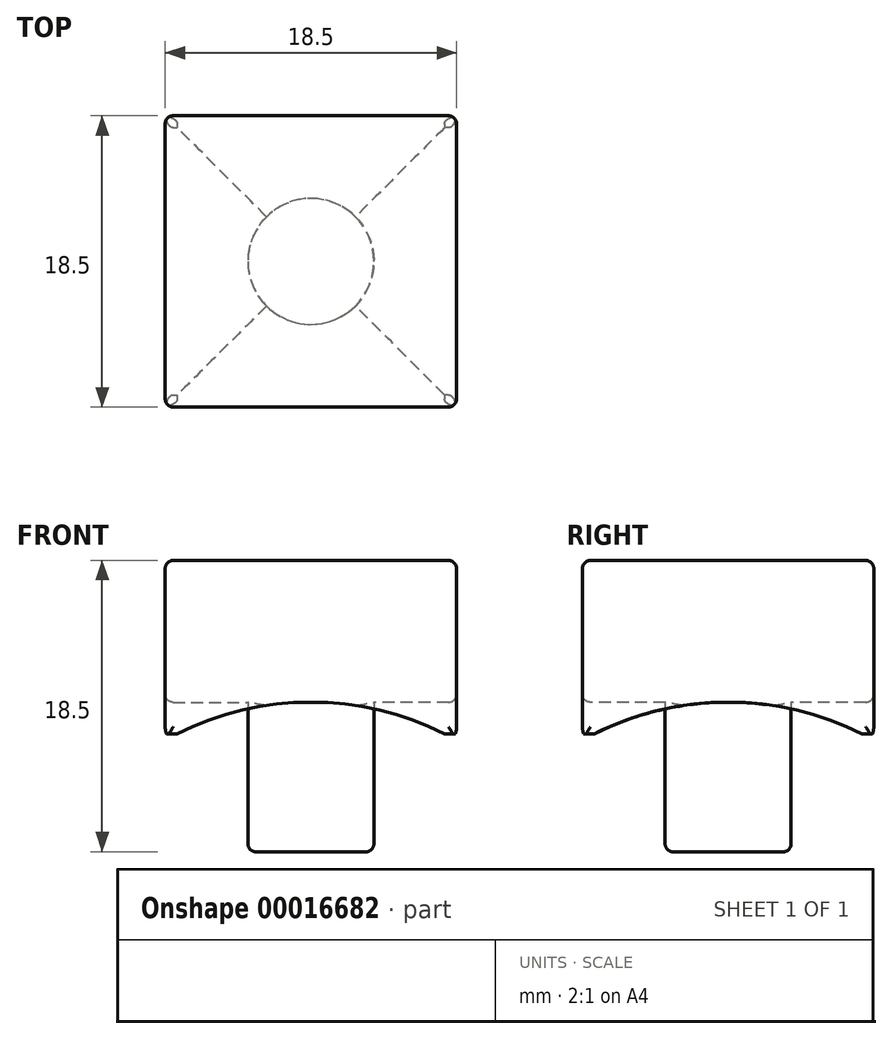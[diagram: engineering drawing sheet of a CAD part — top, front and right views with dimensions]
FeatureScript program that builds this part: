
annotation { "Feature Type Name" : "Feature", "Feature Type Description" : "" }
export const myFeature = defineFeature(function(context is Context, id is Id, definition is map)
    precondition{}
    {
        {
            var Q0;
            Q0=qCreatedBy(makeId("Front.planeOp"),FACE);
            var sketch = newSketch(context, id + "F0", { "sketchPlane" : qUnion([Q0])});
            skLineSegment(sketch, "E0.rect.bottom", {"start": v(9.25, 5.5) * mm, "end": v(-9.25, 5.5) * mm});
            skLineSegment(sketch, "E0.rect.top", {"start": v(9.25, -5.5) * mm, "end": v(-9.25, -5.5) * mm});
            skLineSegment(sketch, "E0.rect.left", {"start": v(9.25, 5.5) * mm, "end": v(9.25, -5.5) * mm});
            skLineSegment(sketch, "E0.rect.right", {"start": v(-9.25, 5.5) * mm, "end": v(-9.25, -5.5) * mm});
            skPoint(sketch, "E0.rect.middle", {"position": v(0, 0) * mm});
            skSolve(sketch);
        }
        {
            var Q0;
            Q0=makeQuery(id+"F0.imprint","IMPRINT",FACE,{"disambiguationData":[TD([[makeQuery(id+"F0.imprint","IMPRINT",EDGE,{"derivedFrom":sQuery(id+"F0.wireOp",EDGE,"E0.rect.bottom")}),1.0]])]});
            extrude(context, id + "F1", {"entities" : qUnion([Q0]), "oppositeDirection" : true, "depth" : 9.25 * mm});
        }
        {
            var Q0;
            Q0 = qSketchRegion(id + "F0", true);
            extrude(context, id + "F2", {"entities" : qUnion([Q0]), "operationType" : NewBodyOperationType.ADD, "depth" : 9.25 * mm});
        }
        {
            var Q0;
            Q0=qCreatedBy(makeId("Front.planeOp"),FACE);
            var sketch = newSketch(context, id + "F3", { "sketchPlane" : qUnion([Q0])});
            skPoint(sketch, "E1", {"position": v(0, -3.5) * mm});
            skCircle(sketch, "E2", {"center": v(0, -22.5) * mm, "radius": 19 * mm});
            skSolve(sketch);
        }
        {
            var Q0;
            Q0=qCreatedBy(makeId("Right.planeOp"),FACE);
            var sketch = newSketch(context, id + "F4", { "sketchPlane" : qUnion([Q0])});
            skPoint(sketch, "E3", {"position": v(0, -3.5) * mm});
            skCircle(sketch, "E4", {"center": v(0, -22.5) * mm, "radius": 19 * mm});
            skSolve(sketch);
        }
        {
            var Q0;
            Q0 = qSketchRegion(id + "F9", true);
            var Q1;
            Q1 = qSketchRegion(id + "F3", true);
            extrude(context, id + "F5", {"entities" : qUnion([Q0, Q1]), "operationType" : NewBodyOperationType.REMOVE, "oppositeDirection" : true, "depth" : 25.4 * mm});
        }
        {
            var Q0;
            Q0 = qSketchRegion(id + "F3", true);
            extrude(context, id + "F6", {"entities" : qUnion([Q0]), "operationType" : NewBodyOperationType.REMOVE, "depth" : 25.4 * mm});
        }
        {
            var Q0;
            Q0 = qSketchRegion(id + "F4", true);
            extrude(context, id + "F7", {"entities" : qUnion([Q0]), "operationType" : NewBodyOperationType.REMOVE, "oppositeDirection" : true, "depth" : 25.4 * mm});
        }
        {
            var Q0;
            Q0 = qSketchRegion(id + "F4", true);
            extrude(context, id + "F8", {"entities" : qUnion([Q0]), "operationType" : NewBodyOperationType.REMOVE, "depth" : 25.4 * mm});
        }
        {
            var Q0;
            {var subQ0=sQuery(id+"F0.wireOp",EDGE,"E0.rect.top");Q0=makeQuery(id+"F2.boolean.opBoolean","MERGE",FACE,{"derivedFrom":[makeQuery(id+"F1.opExtrude","SWEPT_FACE",FACE,{"disambiguationData":[OSD([subQ0])]}),makeQuery(id+"F2.opExtrude","SWEPT_FACE",FACE,{"disambiguationData":[OSD([subQ0])]})]});}
            var sketch = newSketch(context, id + "F9", { "sketchPlane" : qUnion([Q0])});
            skCircle(sketch, "E5", {"center": v(0, 0) * mm, "radius": 4 * mm});
            skSolve(sketch);
        }
        {
            var Q0;
            Q0 = qSketchRegion(id + "F9", true);
            extrude(context, id + "F10", {"entities" : qUnion([Q0]), "operationType" : NewBodyOperationType.ADD, "oppositeDirection" : true, "depth" : 3.46 * mm});
        }
        {
            var Q0;
            Q0=makeQuery(id+"F10.opExtrude","CAP_FACE",FACE,{"disambiguationData":[OSD([sQuery(id+"F9.wireOp",EDGE,"E5")])],"isStart":true});
            extrude(context, id + "F11", {"entities" : qUnion([Q0]), "operationType" : NewBodyOperationType.ADD, "depth" : 7.5 * mm});
        }
        {
            var Q0;
            Q0=makeQuery(id+"F2.opExtrude","CAP_EDGE",EDGE,{"disambiguationData":[OSD([sQuery(id+"F0.wireOp",EDGE,"E0.rect.left")])],"isStart":false});
            var Q1;
            Q1=makeQuery(id+"F2.opExtrude","CAP_EDGE",EDGE,{"disambiguationData":[OSD([sQuery(id+"F0.wireOp",EDGE,"E0.rect.bottom")])],"isStart":false});
            var Q2;
            {var subQ0=sQuery(id+"F0.wireOp",EDGE,"E0.rect.bottom");var subQ1=sQuery(id+"F0.wireOp",EDGE,"E0.rect.left");Q2=makeQuery(id+"F2.boolean.opBoolean","MERGE",EDGE,{"derivedFrom":[makeQuery(id+"F1.opExtrude","SWEPT_EDGE",EDGE,{"disambiguationData":[OSD([subQ0,subQ1])]}),makeQuery(id+"F2.opExtrude","SWEPT_EDGE",EDGE,{"disambiguationData":[OSD([subQ0,subQ1])]})]});}
            var Q3;
            Q3=makeQuery(id+"F1.opExtrude","CAP_EDGE",EDGE,{"disambiguationData":[OSD([sQuery(id+"F0.wireOp",EDGE,"E0.rect.bottom")])],"isStart":false});
            var Q4;
            {var subQ0=sQuery(id+"F0.wireOp",EDGE,"E0.rect.bottom");var subQ1=sQuery(id+"F0.wireOp",EDGE,"E0.rect.right");Q4=makeQuery(id+"F2.boolean.opBoolean","MERGE",EDGE,{"derivedFrom":[makeQuery(id+"F1.opExtrude","SWEPT_EDGE",EDGE,{"disambiguationData":[OSD([subQ0,subQ1])]}),makeQuery(id+"F2.opExtrude","SWEPT_EDGE",EDGE,{"disambiguationData":[OSD([subQ0,subQ1])]})]});}
            var Q5;
            Q5=makeQuery(id+"F2.opExtrude","CAP_EDGE",EDGE,{"disambiguationData":[OSD([sQuery(id+"F0.wireOp",EDGE,"E0.rect.right")])],"isStart":false});
            var Q6;
            Q6=makeQuery(id+"F1.opExtrude","CAP_EDGE",EDGE,{"disambiguationData":[OSD([sQuery(id+"F0.wireOp",EDGE,"E0.rect.left")])],"isStart":false});
            var Q7;
            Q7=makeQuery(id+"F1.opExtrude","CAP_EDGE",EDGE,{"disambiguationData":[OSD([sQuery(id+"F0.wireOp",EDGE,"E0.rect.right")])],"isStart":false});
            var Q8;
            Q8=makeQuery(id+"F11.opExtrude","CAP_EDGE",EDGE,{"disambiguationData":[OSD([sQuery(id+"F9.wireOp",EDGE,"E5")])],"isStart":false});
            var Q9;
            Q9=makeQuery(id+"F6.boolean.opBoolean","INTERSECT",EDGE,{"derivedFrom":[makeQuery(id+"F2.opExtrude","CAP_FACE",FACE,{"disambiguationData":[OSD([sQuery(id+"F0.wireOp",EDGE,"E0.rect.bottom"),sQuery(id+"F0.wireOp",EDGE,"E0.rect.top"),sQuery(id+"F0.wireOp",EDGE,"E0.rect.left"),sQuery(id+"F0.wireOp",EDGE,"E0.rect.right")])],"isStart":false}),makeQuery(id+"F6.opExtrude","SWEPT_FACE",FACE,{"disambiguationData":[OSD([sQuery(id+"F3.wireOp",EDGE,"E2")])]})]});
            var Q10;
            {var subQ0=sQuery(id+"F0.wireOp",EDGE,"E0.rect.right");Q10=makeQuery(id+"F7.boolean.opBoolean","INTERSECT",EDGE,{"derivedFrom":[makeQuery(id+"F2.boolean.opBoolean","MERGE",FACE,{"derivedFrom":[makeQuery(id+"F1.opExtrude","SWEPT_FACE",FACE,{"disambiguationData":[OSD([subQ0])]}),makeQuery(id+"F2.opExtrude","SWEPT_FACE",FACE,{"disambiguationData":[OSD([subQ0])]})]}),makeQuery(id+"F7.opExtrude","SWEPT_FACE",FACE,{"disambiguationData":[OSD([sQuery(id+"F4.wireOp",EDGE,"E4")])]})]});}
            var Q11;
            {var subQ0=sQuery(id+"F0.wireOp",EDGE,"E0.rect.left");Q11=makeQuery(id+"F8.boolean.opBoolean","INTERSECT",EDGE,{"derivedFrom":[makeQuery(id+"F2.boolean.opBoolean","MERGE",FACE,{"derivedFrom":[makeQuery(id+"F1.opExtrude","SWEPT_FACE",FACE,{"disambiguationData":[OSD([subQ0])]}),makeQuery(id+"F2.opExtrude","SWEPT_FACE",FACE,{"disambiguationData":[OSD([subQ0])]})]}),makeQuery(id+"F8.opExtrude","SWEPT_FACE",FACE,{"disambiguationData":[OSD([sQuery(id+"F4.wireOp",EDGE,"E4")])]})]});}
            var Q12;
            Q12=makeQuery(id+"F5.boolean.opBoolean","INTERSECT",EDGE,{"derivedFrom":[makeQuery(id+"F1.opExtrude","CAP_FACE",FACE,{"disambiguationData":[OSD([sQuery(id+"F0.wireOp",EDGE,"E0.rect.bottom"),sQuery(id+"F0.wireOp",EDGE,"E0.rect.top"),sQuery(id+"F0.wireOp",EDGE,"E0.rect.left"),sQuery(id+"F0.wireOp",EDGE,"E0.rect.right")])],"isStart":false}),makeQuery(id+"F5.opExtrude","SWEPT_FACE",FACE,{"disambiguationData":[OSD([sQuery(id+"F3.wireOp",EDGE,"E2")])]})]});
            fillet(context, id + "F12", {"entities" : qUnion([Q0, Q1, Q2, Q3, Q4, Q5, Q6, Q7, Q8, Q9, Q10, Q11, Q12]), "radius" : .5 * mm, "tangentPropagation" : true, "allowEdgeOverflow" : false});
        }
    });
